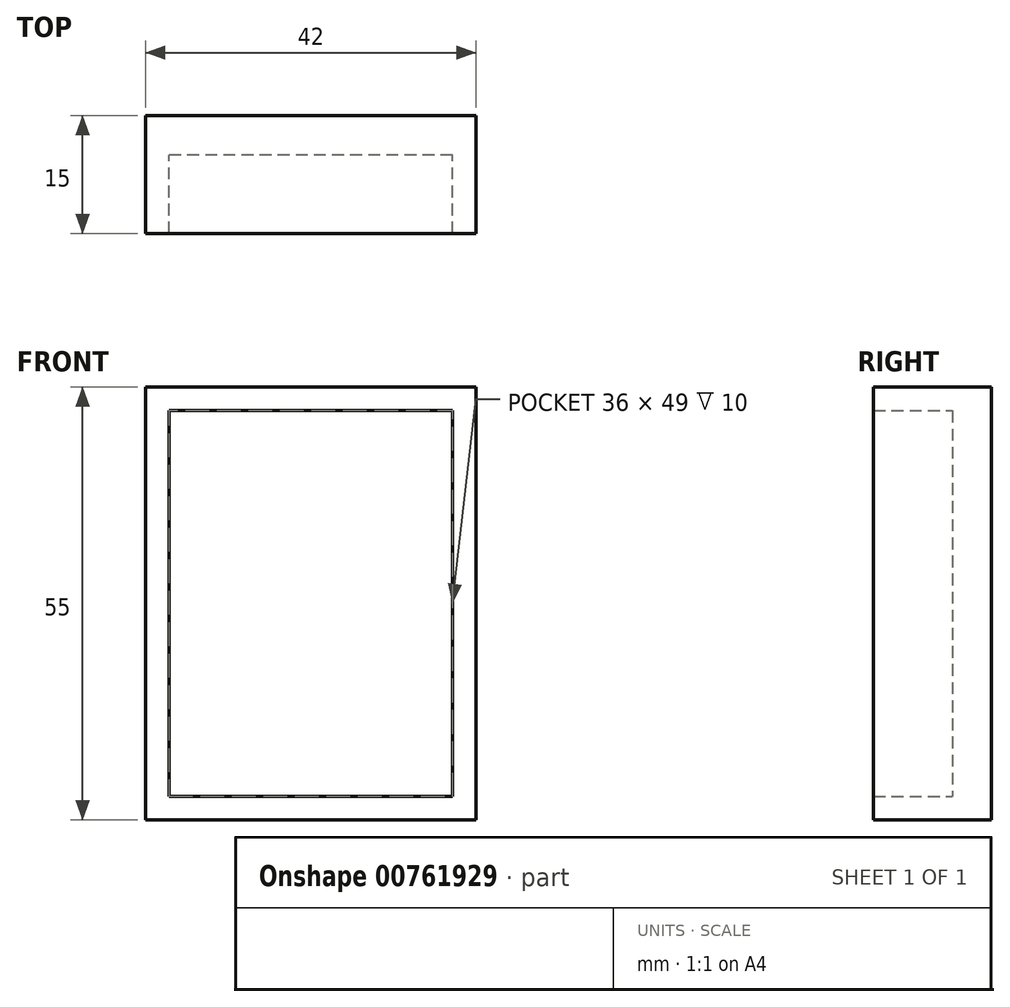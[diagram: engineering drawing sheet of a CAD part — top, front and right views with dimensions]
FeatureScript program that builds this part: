
annotation { "Feature Type Name" : "Feature", "Feature Type Description" : "" }
export const myFeature = defineFeature(function(context is Context, id is Id, definition is map)
    precondition{}
    {
        {
            var Q0;
            Q0=qCreatedBy(makeId("Front.planeOp"),FACE);
            var sketch = newSketch(context, id + "F0", { "sketchPlane" : qUnion([Q0])});
            skLineSegment(sketch, "E0.bottom", {"start": v(18, 24.5) * mm, "end": v(-18, 24.5) * mm});
            skLineSegment(sketch, "E0.top", {"start": v(18, -24.5) * mm, "end": v(-18, -24.5) * mm});
            skLineSegment(sketch, "E0.left", {"start": v(18, 24.5) * mm, "end": v(18, -24.5) * mm});
            skLineSegment(sketch, "E0.right", {"start": v(-18, 24.5) * mm, "end": v(-18, -24.5) * mm});
            skPoint(sketch, "E0.middle", {"position": v(0, 0) * mm});
            skLineSegment(sketch, "E1.0", {"start": v(21, 27.5) * mm, "end": v(-21, 27.5) * mm});
            skLineSegment(sketch, "E2.0", {"start": v(-21, 27.5) * mm, "end": v(-21, -27.5) * mm});
            skLineSegment(sketch, "E3.0", {"start": v(21, -27.5) * mm, "end": v(-21, -27.5) * mm});
            skLineSegment(sketch, "E4.0", {"start": v(21, 27.5) * mm, "end": v(21, -27.5) * mm});
            skSolve(sketch);
        }
        {
            var Q0;
            Q0=makeQuery(id+"F0.imprint","IMPRINT",FACE,{"disambiguationData":[TD([[makeQuery(id+"F0.imprint","IMPRINT",EDGE,{"derivedFrom":sQuery(id+"F0.wireOp",EDGE,"E0.bottom")}),-1.0]])]});
            var Q1;
            Q1=makeQuery(id+"F0.imprint","IMPRINT",FACE,{"disambiguationData":[TD([[makeQuery(id+"F0.imprint","IMPRINT",EDGE,{"derivedFrom":sQuery(id+"F0.wireOp",EDGE,"E0.bottom")}),1.0]])]});
            extrude(context, id + "F1", {"entities" : qUnion([Q0, Q1]), "oppositeDirection" : true, "depth" : 5 * mm, "offsetDistance" : 25 * mm});
        }
        {
            var Q0;
            Q0=makeQuery(id+"F0.imprint","IMPRINT",FACE,{"disambiguationData":[TD([[makeQuery(id+"F0.imprint","IMPRINT",EDGE,{"derivedFrom":sQuery(id+"F0.wireOp",EDGE,"E0.bottom")}),-1.0]])]});
            extrude(context, id + "F2", {"entities" : qUnion([Q0]), "operationType" : NewBodyOperationType.ADD, "depth" : 10 * mm, "offsetDistance" : 25 * mm});
        }
    });
